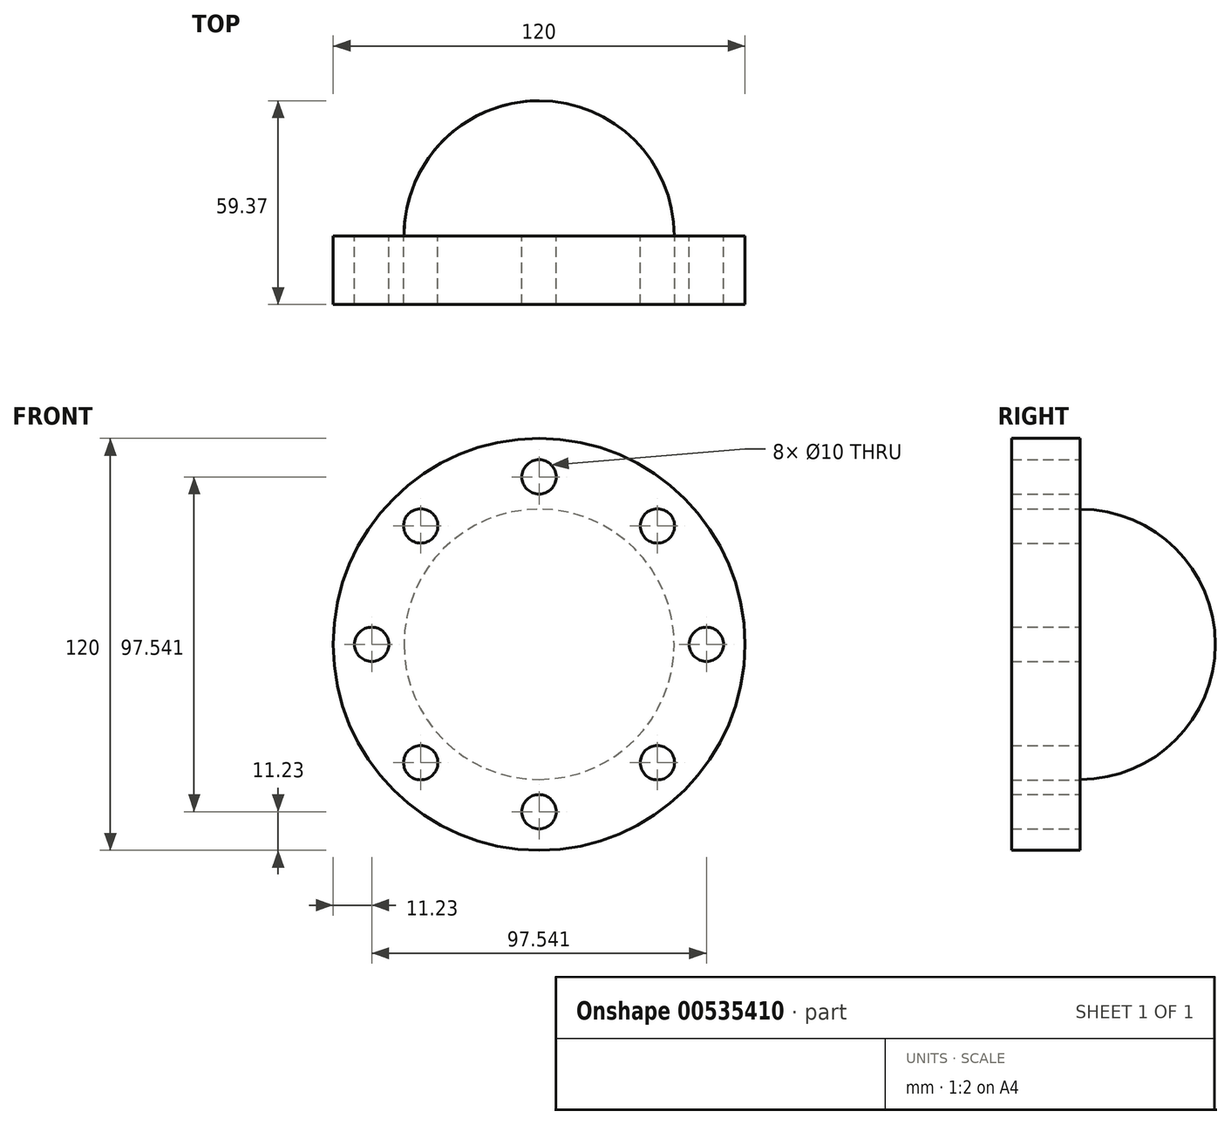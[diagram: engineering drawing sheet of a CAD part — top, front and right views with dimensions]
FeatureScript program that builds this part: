
annotation { "Feature Type Name" : "Feature", "Feature Type Description" : "" }
export const myFeature = defineFeature(function(context is Context, id is Id, definition is map)
    precondition{}
    {
        {
            var Q0;
            Q0=qCreatedBy(makeId("Front.planeOp"),FACE);
            var sketch = newSketch(context, id + "F0", { "sketchPlane" : qUnion([Q0])});
            skCircle(sketch, "E0", {"center": v(0, 0) * mm, "radius": 60 * mm});
            skCircle(sketch, "E1", {"center": v(0, 48.77) * mm, "radius": 5 * mm});
            skCircle(sketch, "E2.1.0", {"center": v(-34.49, 34.49) * mm, "radius": 5 * mm});
            skCircle(sketch, "E2.2.0", {"center": v(-48.77, 0) * mm, "radius": 5 * mm});
            skCircle(sketch, "E2.3.0", {"center": v(-34.49, -34.49) * mm, "radius": 5 * mm});
            skCircle(sketch, "E2.4.0", {"center": v(0, -48.77) * mm, "radius": 5 * mm});
            skCircle(sketch, "E2.5.0", {"center": v(34.49, -34.49) * mm, "radius": 5 * mm});
            skCircle(sketch, "E2.6.0", {"center": v(48.77, 0) * mm, "radius": 5 * mm});
            skCircle(sketch, "E2.7.0", {"center": v(34.49, 34.49) * mm, "radius": 5 * mm});
            skSolve(sketch);
        }
        {
            var Q0;
            Q0=makeQuery(id+"F0.imprint","IMPRINT",FACE,{"disambiguationData":[TD([[makeQuery(id+"F0.imprint","IMPRINT",EDGE,{"derivedFrom":sQuery(id+"F0.wireOp",EDGE,"E0")}),1.0]])]});
            extrude(context, id + "F1", {"entities" : qUnion([Q0]), "depth" : 20 * mm, "offsetDistance" : 25.4 * mm});
        }
        {
            var Q0;
            Q0=qCreatedBy(makeId("Top.planeOp"),FACE);
            var sketch = newSketch(context, id + "F2", { "sketchPlane" : qUnion([Q0])});
            skArc(sketch, "E3", {"start": v(0, 39.37) * mm, "mid": v(-27.84, 27.84) * mm, "end": v(-39.37, 0) * mm});
            skLineSegment(sketch, "E4", {"start": v(60, 0) * mm, "end": v(60, -20) * mm});
            skLineSegment(sketch, "E5", {"start": v(-60, -20) * mm, "end": v(-60, 0) * mm});
            skLineSegment(sketch, "E6", {"start": v(0, 39.37) * mm, "end": v(0, 0) * mm});
            skLineSegment(sketch, "E7", {"start": v(-39.37, 0) * mm, "end": v(0, 0) * mm});
            skSolve(sketch);
        }
        {
            var Q0;
            Q0 = qSketchRegion(id + "F2", true);
            var Q1;
            Q1=sQuery(id+"F2.wireOp",EDGE,"E6");
            revolve(context, id + "F3", {"operationType" : NewBodyOperationType.ADD, "entities" : qUnion([Q0]), "axis" : qUnion([Q1]), "revolveType" : RevolveType.FULL, "oppositeDirection" : true});
        }
    });
